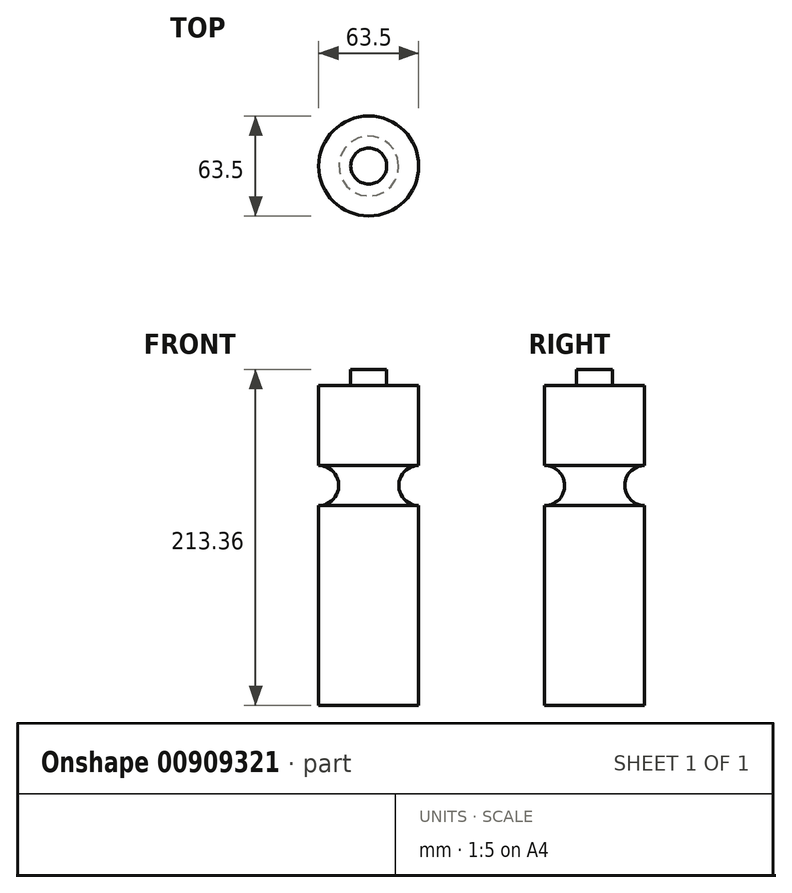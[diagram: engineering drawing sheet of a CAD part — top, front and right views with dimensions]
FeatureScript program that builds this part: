
annotation { "Feature Type Name" : "Feature", "Feature Type Description" : "" }
export const myFeature = defineFeature(function(context is Context, id is Id, definition is map)
    precondition{}
    {
        {
            var Q0;
            Q0=qCreatedBy(makeId("Front.planeOp"),FACE);
            var sketch = newSketch(context, id + "F0", { "sketchPlane" : qUnion([Q0])});
            skLineSegment(sketch, "E0", {"start": v(0, 0) * mm, "end": v(0, 127) * mm});
            skArc(sketch, "E1", {"start": v(0, 127) * mm, "mid": v(-12.7, 139.7) * mm, "end": v(0, 152.4) * mm});
            skLineSegment(sketch, "E2", {"start": v(0, 152.4) * mm, "end": v(0, 203.2) * mm});
            skLineSegment(sketch, "E3", {"start": v(0, 0) * mm, "end": v(-31.75, 0) * mm});
            skLineSegment(sketch, "E4", {"start": v(-31.75, 203.2) * mm, "end": v(0, 203.2) * mm});
            skLineSegment(sketch, "E5", {"start": v(-31.75, 203.2) * mm, "end": v(-31.75, 0) * mm});
            skSolve(sketch);
        }
        {
            var Q0;
            Q0=makeQuery(id+"F0.imprint","IMPRINT",FACE,{"disambiguationData":[TD([[makeQuery(id+"F0.imprint","IMPRINT",EDGE,{"derivedFrom":sQuery(id+"F0.wireOp",EDGE,"E0")}),1.0]])]});
            var Q1;
            Q1=sQuery(id+"F0.wireOp",EDGE,"E5");
            revolve(context, id + "F1", {"surfaceOperationType" : NewSurfaceOperationType.NEW, "entities" : qUnion([Q0]), "axis" : qUnion([Q1]), "revolveType" : RevolveType.FULL});
        }
        {
            var Q0;
            Q0=makeQuery(id+"F1.opRevolve","SWEPT_FACE",FACE,{"disambiguationData":[OSD([sQuery(id+"F0.wireOp",EDGE,"E4")])]});
            var sketch = newSketch(context, id + "F2", { "sketchPlane" : qUnion([Q0])});
            skCircle(sketch, "E6", {"center": v(-31.75, 0) * mm, "radius": 11.43 * mm});
            skSolve(sketch);
        }
        {
            var Q0;
            Q0=makeQuery(id+"F2.imprint","IMPRINT",FACE,{"disambiguationData":[TD([[makeQuery(id+"F2.imprint","IMPRINT",EDGE,{"derivedFrom":sQuery(id+"F2.wireOp",EDGE,"E6")}),1.0]])]});
            extrude(context, id + "F3", {"entities" : qUnion([Q0]), "operationType" : NewBodyOperationType.ADD, "depth" : 10.16 * mm, "offsetDistance" : 25.4 * mm});
        }
    });
